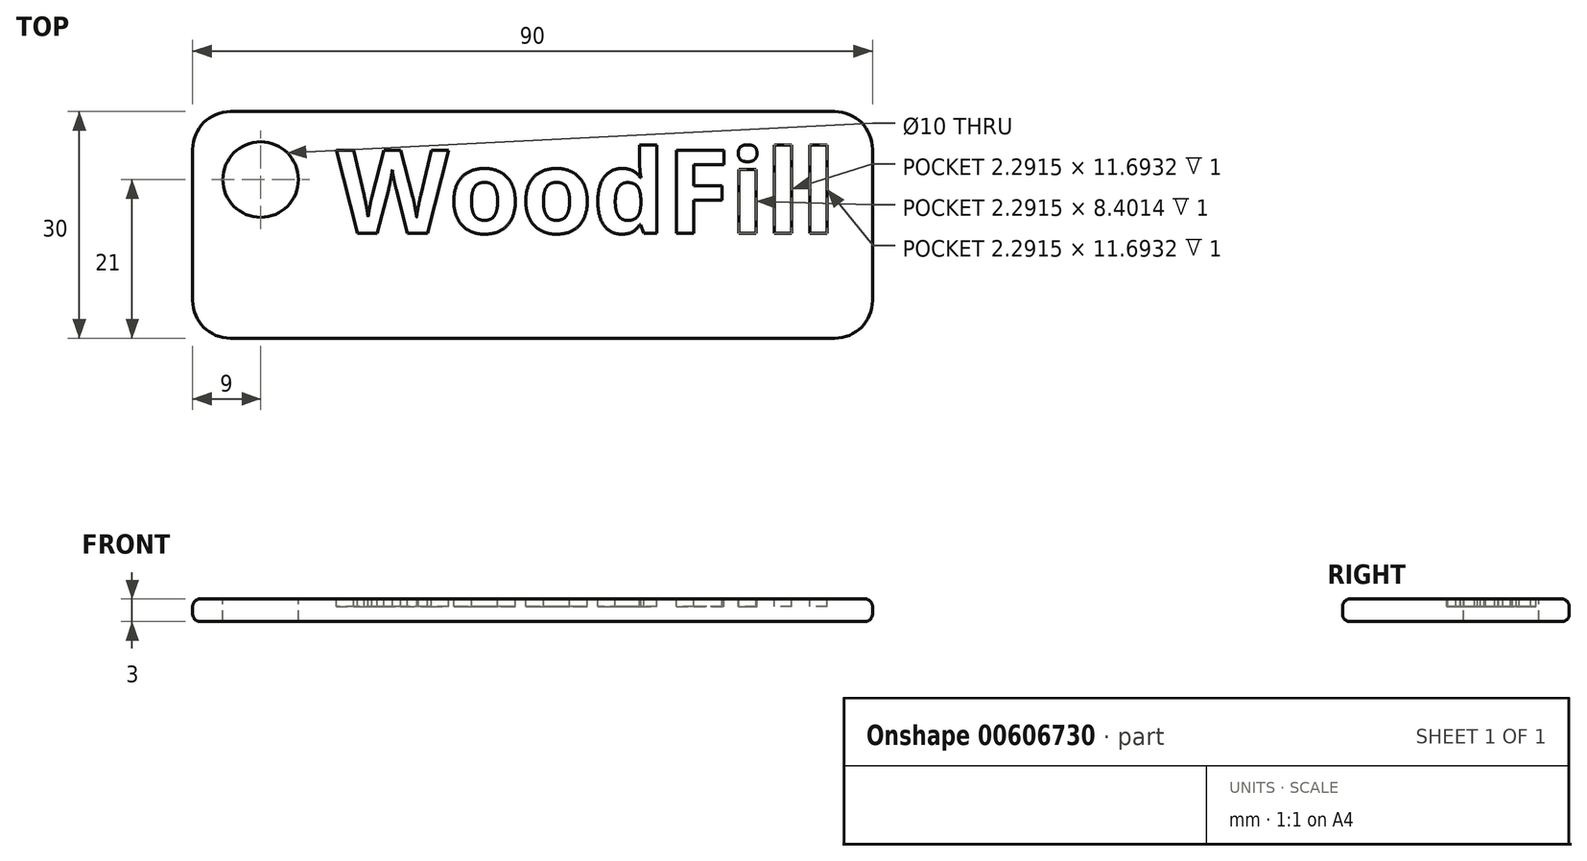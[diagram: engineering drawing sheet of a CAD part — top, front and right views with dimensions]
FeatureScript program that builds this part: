
annotation { "Feature Type Name" : "Feature", "Feature Type Description" : "" }
export const myFeature = defineFeature(function(context is Context, id is Id, definition is map)
    precondition{}
    {
        {
            var Q0;
            Q0=qCreatedBy(makeId("Top.planeOp"),FACE);
            var sketch = newSketch(context, id + "F0", { "sketchPlane" : qUnion([Q0])});
            skLineSegment(sketch, "E0.bottom", {"start": v(-45, 15) * mm, "end": v(45, 15) * mm});
            skLineSegment(sketch, "E0.top", {"start": v(-45, -15) * mm, "end": v(45, -15) * mm});
            skLineSegment(sketch, "E0.left", {"start": v(-45, 15) * mm, "end": v(-45, -15) * mm});
            skLineSegment(sketch, "E0.right", {"start": v(45, 15) * mm, "end": v(45, -15) * mm});
            skLineSegment(sketch, "E1", {"start": v(-45, 15) * mm, "end": v(45, -15) * mm, "construction": true});
            skSolve(sketch);
        }
        {
            var Q0;
            Q0=makeQuery(id+"F0.imprint","IMPRINT",FACE,{"disambiguationData":[TD([[makeQuery(id+"F0.imprint","IMPRINT",EDGE,{"derivedFrom":sQuery(id+"F0.wireOp",EDGE,"E0.bottom")}),-1.0]])]});
            extrude(context, id + "F1", {"entities" : qUnion([Q0]), "depth" : 3 * mm});
        }
        {
            var Q0;
            Q0=makeQuery(id+"F1.opExtrude","CAP_FACE",FACE,{"disambiguationData":[OSD([sQuery(id+"F0.wireOp",EDGE,"E0.bottom"),sQuery(id+"F0.wireOp",EDGE,"E0.top"),sQuery(id+"F0.wireOp",EDGE,"E0.left"),sQuery(id+"F0.wireOp",EDGE,"E0.right")])],"isStart":false});
            var Q1;
            Q1=makeQuery(id+"F1.opExtrude","CAP_FACE",FACE,{"disambiguationData":[OSD([sQuery(id+"F0.wireOp",EDGE,"E0.bottom"),sQuery(id+"F0.wireOp",EDGE,"E0.top"),sQuery(id+"F0.wireOp",EDGE,"E0.left"),sQuery(id+"F0.wireOp",EDGE,"E0.right")])],"isStart":true});
            fillet(context, id + "F2", {"entities" : qUnion([Q0, Q1]), "radius" : 1 * mm, "tangentPropagation" : true, "allowEdgeOverflow" : false});
        }
        {
            var Q0;
            Q0=makeQuery(id+"F1.opExtrude","SWEPT_EDGE",EDGE,{"disambiguationData":[OSD([sQuery(id+"F0.wireOp",EDGE,"E0.top"),sQuery(id+"F0.wireOp",EDGE,"E0.right")])]});
            var Q1;
            Q1=makeQuery(id+"F1.opExtrude","SWEPT_EDGE",EDGE,{"disambiguationData":[OSD([sQuery(id+"F0.wireOp",EDGE,"E0.bottom"),sQuery(id+"F0.wireOp",EDGE,"E0.right")])]});
            var Q2;
            Q2=makeQuery(id+"F1.opExtrude","SWEPT_EDGE",EDGE,{"disambiguationData":[OSD([sQuery(id+"F0.wireOp",EDGE,"E0.bottom"),sQuery(id+"F0.wireOp",EDGE,"E0.left")])]});
            var Q3;
            Q3=makeQuery(id+"F1.opExtrude","SWEPT_EDGE",EDGE,{"disambiguationData":[OSD([sQuery(id+"F0.wireOp",EDGE,"E0.top"),sQuery(id+"F0.wireOp",EDGE,"E0.left")])]});
            fillet(context, id + "F3", {"entities" : qUnion([Q0, Q1, Q2, Q3]), "radius" : 5 * mm, "tangentPropagation" : true, "allowEdgeOverflow" : false});
        }
        {
            var Q0;
            {var subQ0=sQuery(id+"F0.wireOp",EDGE,"E0.left");var subQ2=sQuery(id+"F0.wireOp",EDGE,"E0.bottom");var subQ4=sQuery(id+"F0.wireOp",EDGE,"E0.right");var subQ6=sQuery(id+"F0.wireOp",EDGE,"E0.top");Q0=makeQuery(id+"FmQCBBX3Ub0qneL_1.boolean.opBoolean","SPLIT",FACE,{"disambiguationData":[TD([makeQuery(id+"FmQCBBX3Ub0qneL_1.opExtrude","SWEPT_FACE",FACE,{"disambiguationData":[OSD([sQuery(id+"FOCoeRmDbjhRCuz_1.wireOp",EDGE,"4a1fb44a-e7be-4e23-9449-000d953c446c.sketch_text.stroke-0")])]})])],"derivedFrom":makeQuery(id+"F1.opExtrude","CAP_FACE",FACE,{"disambiguationData":[OSD([subQ2,subQ6,subQ0,subQ4])],"isStart":false})});}
            var sketch = newSketch(context, id + "F4", { "sketchPlane" : qUnion([Q0])});
            skCircle(sketch, "E2", {"center": v(-36, 6) * mm, "radius": 5 * mm});
            skSolve(sketch);
        }
        {
            var Q0;
            Q0=qSketchRegion(id+"F4",true);
            extrude(context, id + "F5", {"entities" : qUnion([Q0]), "operationType" : NewBodyOperationType.REMOVE, "oppositeDirection" : true, "depth" : 3 * mm});
        }
        {
            var Q0;
            Q0=makeQuery(id+"F1.opExtrude","CAP_FACE",FACE,{"disambiguationData":[OSD([sQuery(id+"F0.wireOp",EDGE,"E0.bottom"),sQuery(id+"F0.wireOp",EDGE,"E0.top"),sQuery(id+"F0.wireOp",EDGE,"E0.left"),sQuery(id+"F0.wireOp",EDGE,"E0.right")])],"isStart":false});
            var sketch = newSketch(context, id + "F6", { "sketchPlane" : qUnion([Q0])});
            skText(sketch, "E3", { "text": "WoodFill", "fontName": "OpenSans-Bold.ttf"});
            const initialGuessF6  = {"E3": [-0.026, -0.00108, 1, 0, 0.01108]};
            skSetInitialGuess(sketch, initialGuessF6);
            skSolve(sketch);
        }
        {
            var Q0;
            Q0=qSketchRegion(id+"F6",true);
            extrude(context, id + "F7", {"entities" : qUnion([Q0]), "operationType" : NewBodyOperationType.REMOVE, "oppositeDirection" : true, "depth" : 1 * mm});
        }
    });
